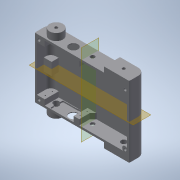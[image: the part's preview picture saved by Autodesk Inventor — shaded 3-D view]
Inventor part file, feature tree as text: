
AUTODESK INVENTOR PART (.ipt)
format: ipt  version: 2020 (Build 240168000, 168)  size: 507,392 bytes
history: native  units: mm
features: reference x30, extrude x17, sketch x14, other x12, mirror x7, hole x3, projected_geometry x3, chamfer x1
ambient origin geometry x8: Origin, YZ Plane, XZ Plane, XY Plane, X Axis, Y Axis, Z Axis, Center Point
bodies: Body1 (feature_tree)
feature tree (87):
  other  "Bryła1"
  sketch  "Szkic1"
  extrude  "Wyciągnięcie proste1"  Depth=86.0mm
  extrude  "Wyciągnięcie proste2"  Depth=135.0mm
  hole  "Otwór1"  [1 undecoded]
  sketch  "Szkic3"
  extrude  "Wyciągnięcie proste3"  Depth=3.0mm TaperAngle=0.0deg
  extrude  "Wyciągnięcie proste4"  Depth=20.0mm TaperAngle=0.0deg
  other  "Płaszczyzna konstrukcyjna1"
  mirror  "Odbij1"
  other  "Płaszczyzna konstrukcyjna2"
  sketch  "Szkic4"
  extrude  "Wyciągnięcie proste5"  Depth=96.5mm
  extrude  "Wyciągnięcie proste6"  Depth=0.5mm
  mirror  "Odbij2"
  extrude  "Wyciągnięcie proste7"  Depth=10.0mm TaperAngle=0.0deg
  extrude  "Wyciągnięcie proste8"  Depth=7.6mm TaperAngle=0.0deg
  mirror  "Odbij3"
  sketch  "Szkic7"
  extrude  "Wyciągnięcie proste9"  Depth=8.0mm
  extrude  "Wyciągnięcie proste10"  Depth=8.0mm
  chamfer  "Faza1"  Distance=10.0mm
  hole  "Otwór2"  [1 undecoded]
  mirror  "Odbij4"
  sketch  "Szkic10"
  extrude  "Wyciągnięcie proste11"  Depth=0.25mm
  extrude  "Wyciągnięcie proste12"  Depth=0.25mm
  hole  "Otwór3"  [1 undecoded]
  mirror  "Odbij5"
  other  "Płaszczyzna konstrukcyjna3"
  mirror  "Odbij6"
  sketch  "Szkic13"
  extrude  "Wyciągnięcie proste14"  Depth=2.5mm TaperAngle=0.0deg
  extrude  "Wyciągnięcie proste15"  Depth=0.25mm
  extrude  "Wyciągnięcie proste16"  Depth=0.25mm
  extrude  "Wyciągnięcie proste17"  Depth=0.25mm
  extrude  "Wyciągnięcie proste18"  Depth=0.25mm
  mirror  "Odbij7"
  sketch  "Szkic2"
  projected_geometry  "Pętla rzutowana1"
  reference  "Odniesienie1"
  sketch  "Szkic5"
  reference  "Odniesienie2"
  reference  "Odniesienie3"
  sketch  "Szkic6"
  reference  "Odniesienie4"
  reference  "Odniesienie5"
  reference  "Odniesienie6"
  reference  "Odniesienie7"
  reference  "Odniesienie8"
  reference  "Odniesienie9"
  reference  "Odniesienie10"
  reference  "Odniesienie11"
  reference  "Odniesienie12"
  reference  "Odniesienie13"
  reference  "Odniesienie14"
  reference  "Odniesienie15"
  reference  "Odniesienie16"
  reference  "Odniesienie17"
  reference  "Odniesienie18"
  reference  "Odniesienie19"
  reference  "Odniesienie20"
  reference  "Odniesienie21"
  reference  "Odniesienie22"
  reference  "Odniesienie23"
  reference  "Odniesienie24"
  sketch  "Szkic9"
  reference  "Odniesienie25"
  reference  "Odniesienie26"
  reference  "Odniesienie27"
  reference  "Odniesienie28"
  sketch  "Szkic11"
  projected_geometry  "Pętla rzutowana2"
  sketch  "Szkic14"
  sketch  "Szkic15"
  reference  "Odniesienie29"
  reference  "Odniesienie30"
  sketch  "Szkic16"
  projected_geometry  "Pętla rzutowana4"
  other  "<userpath>\Desktop\ScanBot\3d-model\Assembly1.iam"
  other  "Assembly1.iam"
  other  "wheel_MIR:1"
  other  "MG_996R:2"
  other  "Top:1"
  other  "MG_996R:1"
  other  "Medio:1"
  other  "cover-new:1"
note: 3 required parameter values undecoded (feature->parameter linkage not recoverable at this tier; creation-order binding heuristic only, values carry confidence <= 0.55)
